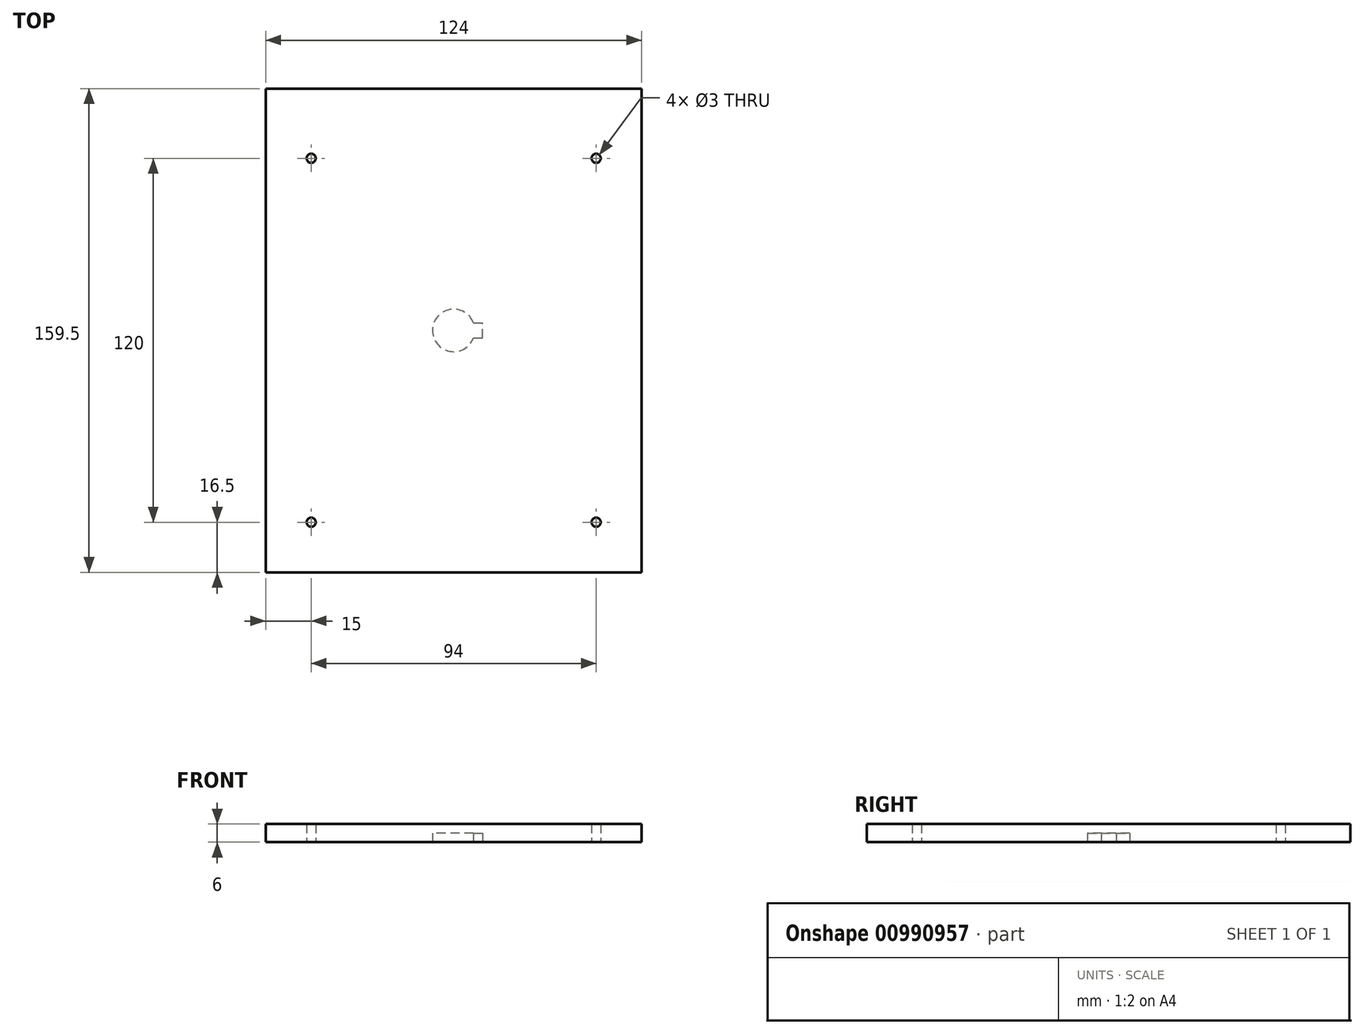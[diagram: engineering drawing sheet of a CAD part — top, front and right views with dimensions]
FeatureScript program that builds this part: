
annotation { "Feature Type Name" : "Feature", "Feature Type Description" : "" }
export const myFeature = defineFeature(function(context is Context, id is Id, definition is map)
    precondition{}
    {
        {
            var Q0;
            Q0=qCreatedBy(makeId("Top.planeOp"),FACE);
            var sketch = newSketch(context, id + "F0", { "sketchPlane" : qUnion([Q0])});
            skLineSegment(sketch, "E0.bottom", {"start": v(62, -79.75) * mm, "end": v(-62, -79.75) * mm});
            skLineSegment(sketch, "E0.top", {"start": v(62, 79.75) * mm, "end": v(-62, 79.75) * mm});
            skLineSegment(sketch, "E0.left", {"start": v(62, -79.75) * mm, "end": v(62, 79.75) * mm});
            skLineSegment(sketch, "E0.right", {"start": v(-62, -79.75) * mm, "end": v(-62, 79.75) * mm});
            skPoint(sketch, "E0.middle", {"position": v(0, 0) * mm});
            skLineSegment(sketch, "E1", {"start": v(0, 79.75) * mm, "end": v(0, -79.75) * mm, "construction": true});
            skCircle(sketch, "E2", {"center": v(-47, 56.75) * mm, "radius": 1.5 * mm});
            skCircle(sketch, "E3.MirrorC", {"center": v(47, 56.75) * mm, "radius": 1.5 * mm});
            skCircle(sketch, "E4", {"center": v(-47, -63.25) * mm, "radius": 1.5 * mm});
            skCircle(sketch, "E5.MirrorC", {"center": v(47, -63.25) * mm, "radius": 1.5 * mm});
            skCircle(sketch, "E6", {"center": v(0, 0) * mm, "radius": 7 * mm});
            skLineSegment(sketch, "E7", {"start": v(-26.4, 0) * mm, "end": v(26.6, 0) * mm, "construction": true});
            skLineSegment(sketch, "E8", {"start": v(6.54, -2.5) * mm, "end": v(9.5, -2.5) * mm});
            skLineSegment(sketch, "E9", {"start": v(9.5, -2.5) * mm, "end": v(9.5, 0) * mm});
            skPoint(sketch, "E10", {"position": v(7, 0) * mm});
            skLineSegment(sketch, "E11.MirrorCS", {"start": v(9.5, 2.5) * mm, "end": v(9.5, 0) * mm});
            skLineSegment(sketch, "E12.MirrorCS", {"start": v(6.54, 2.5) * mm, "end": v(9.5, 2.5) * mm});
            skSolve(sketch);
        }
        {
            var Q0;
            Q0 = qSketchRegion(id + "F0", true);
            var Q1;
            {var subQ0=sQuery(id+"F0.wireOp",EDGE,"E6");var subQ1=makeQuery(id+"F0.imprint","INTERSECT",VERTEX,{"derivedFrom":[subQ0,sQuery(id+"F0.wireOp",EDGE,"E8")]});Q1=makeQuery(id+"F0.imprint","IMPRINT",FACE,{"disambiguationData":[TD([[makeQuery(id+"F0.imprint","IMPRINT",EDGE,{"disambiguationData":[TD([[subQ1,-1.0]])],"derivedFrom":subQ0}),1.0]])]});}
            var Q2;
            {var subQ0=sQuery(id+"F0.wireOp",EDGE,"E8");Q2=makeQuery(id+"F0.imprint","IMPRINT",FACE,{"disambiguationData":[TD([[makeQuery(id+"F0.imprint","IMPRINT",EDGE,{"derivedFrom":subQ0}),1.0]])]});}
            extrude(context, id + "F1", {"entities" : qUnion([Q0, Q1, Q2]), "depth" : 6 * mm, "offsetDistance" : 25 * mm});
        }
        {
            var Q0;
            {var subQ0=sQuery(id+"F0.wireOp",EDGE,"E6");var subQ1=makeQuery(id+"F0.imprint","INTERSECT",VERTEX,{"derivedFrom":[subQ0,sQuery(id+"F0.wireOp",EDGE,"E8")]});Q0=makeQuery(id+"F0.imprint","IMPRINT",FACE,{"disambiguationData":[TD([[makeQuery(id+"F0.imprint","IMPRINT",EDGE,{"disambiguationData":[TD([[subQ1,-1.0]])],"derivedFrom":subQ0}),1.0]])]});}
            var Q1;
            {var subQ0=sQuery(id+"F0.wireOp",EDGE,"E8");Q1=makeQuery(id+"F0.imprint","IMPRINT",FACE,{"disambiguationData":[TD([[makeQuery(id+"F0.imprint","IMPRINT",EDGE,{"derivedFrom":subQ0}),1.0]])]});}
            extrude(context, id + "F2", {"entities" : qUnion([Q0, Q1]), "operationType" : NewBodyOperationType.REMOVE, "depth" : 3 * mm, "offsetDistance" : 25 * mm});
        }
    });
